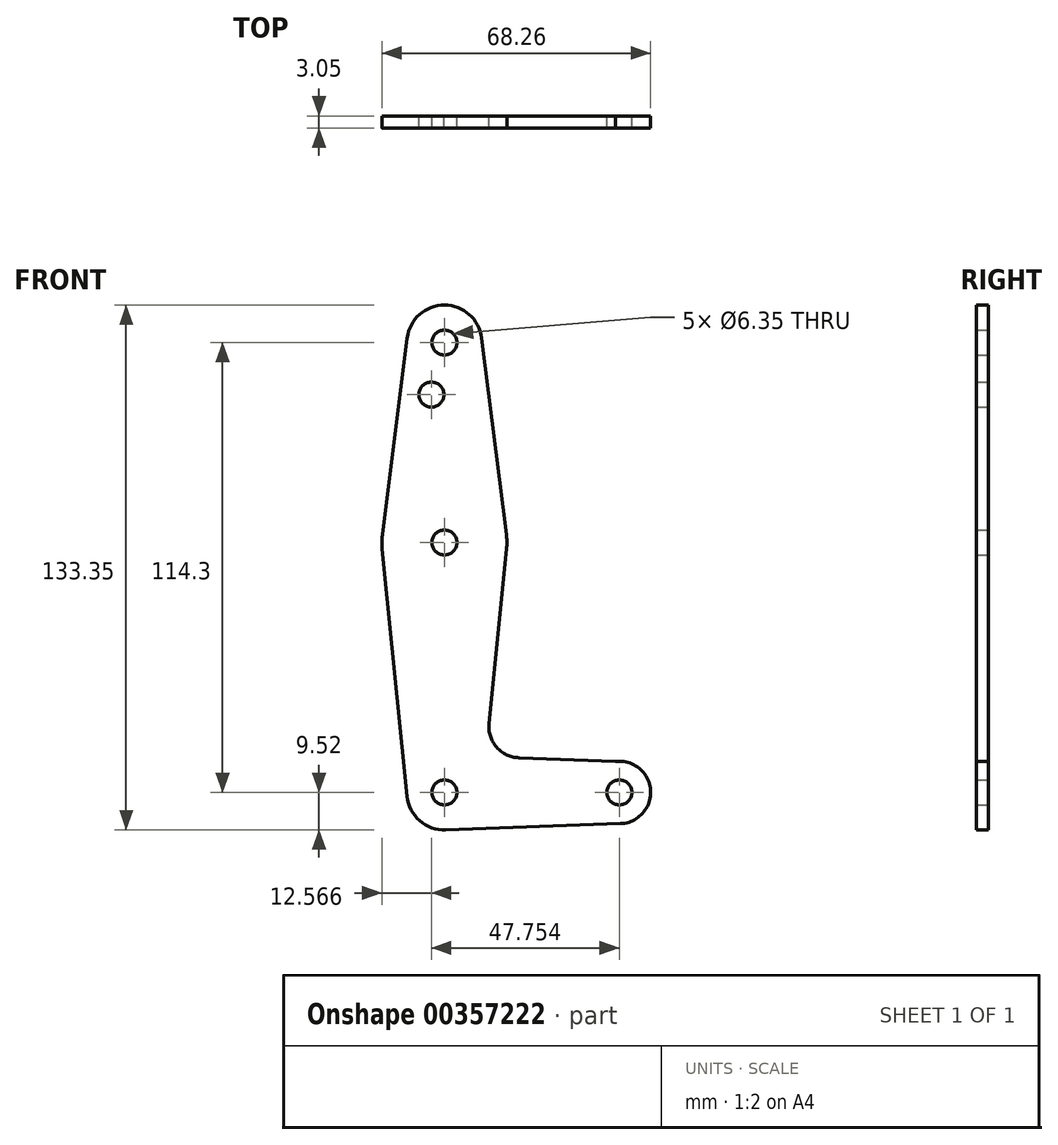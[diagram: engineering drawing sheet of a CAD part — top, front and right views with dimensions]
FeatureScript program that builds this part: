
annotation { "Feature Type Name" : "Feature", "Feature Type Description" : "" }
export const myFeature = defineFeature(function(context is Context, id is Id, definition is map)
    precondition{}
    {
        {
            var Q0;
            Q0=qCreatedBy(makeId("Front.planeOp"),FACE);
            var sketch = newSketch(context, id + "F0", { "sketchPlane" : qUnion([Q0])});
            skCircle(sketch, "E0", {"center": v(0, 0) * mm, "radius": 9.53 * mm});
            skCircle(sketch, "E1", {"center": v(0, 63.5) * mm, "radius": 15.88 * mm});
            skCircle(sketch, "E2", {"center": v(0, 114.3) * mm, "radius": 9.53 * mm});
            skCircle(sketch, "E3", {"center": v(44.45, 0) * mm, "radius": 7.94 * mm});
            skLineSegment(sketch, "E4", {"start": v(0, 114.3) * mm, "end": v(0, 0) * mm});
            skLineSegment(sketch, "E5", {"start": v(0, 63.5) * mm, "end": v(0, 0) * mm});
            skLineSegment(sketch, "E6", {"start": v(0, 114.3) * mm, "end": v(0, 0) * mm, "construction": true});
            skLineSegment(sketch, "E7", {"start": v(0, 63.5) * mm, "end": v(0, 0) * mm, "construction": true});
            skLineSegment(sketch, "E8", {"start": v(0, 0) * mm, "end": v(44.45, 0) * mm, "construction": true});
            skLineSegment(sketch, "E9", {"start": v(9.45, 115.5) * mm, "end": v(15.75, 65.48) * mm});
            skLineSegment(sketch, "E10", {"start": v(-9.48, -0.95) * mm, "end": v(-15.8, 61.91) * mm});
            skLineSegment(sketch, "E11", {"start": v(0.34, -9.52) * mm, "end": v(44.73, -7.93) * mm});
            skLineSegment(sketch, "E12", {"start": v(-9.45, 115.5) * mm, "end": v(-15.75, 65.48) * mm});
            skLineSegment(sketch, "E13", {"start": v(15.8, 61.91) * mm, "end": v(11.34, 17.55) * mm});
            skLineSegment(sketch, "E14", {"start": v(18.94, 8.8) * mm, "end": v(46.04, 7.78) * mm});
            skPoint(sketch, "E15.newPointA", {"position": v(9.57, 0) * mm});
            skArc(sketch, "E15.filletArc", {"start": v(11.34, 17.55) * mm, "mid": v(13.25, 11.53) * mm, "end": v(18.94, 8.8) * mm});
            skCircle(sketch, "E16", {"center": v(0, 114.3) * mm, "radius": 3.18 * mm});
            skCircle(sketch, "E17", {"center": v(0, 63.5) * mm, "radius": 3.18 * mm});
            skCircle(sketch, "E18", {"center": v(44.45, 0) * mm, "radius": 3.18 * mm});
            skCircle(sketch, "E19", {"center": v(-3.3, 101.07) * mm, "radius": 3.18 * mm});
            skCircle(sketch, "E20", {"center": v(0, 0) * mm, "radius": 3.18 * mm});
            skSolve(sketch);
        }
        {
            var Q0;
            Q0 = qSketchRegion(id + "F0", true);
            extrude(context, id + "F1", {"entities" : qUnion([Q0]), "depth" : 3.05 * mm});
        }
    });
